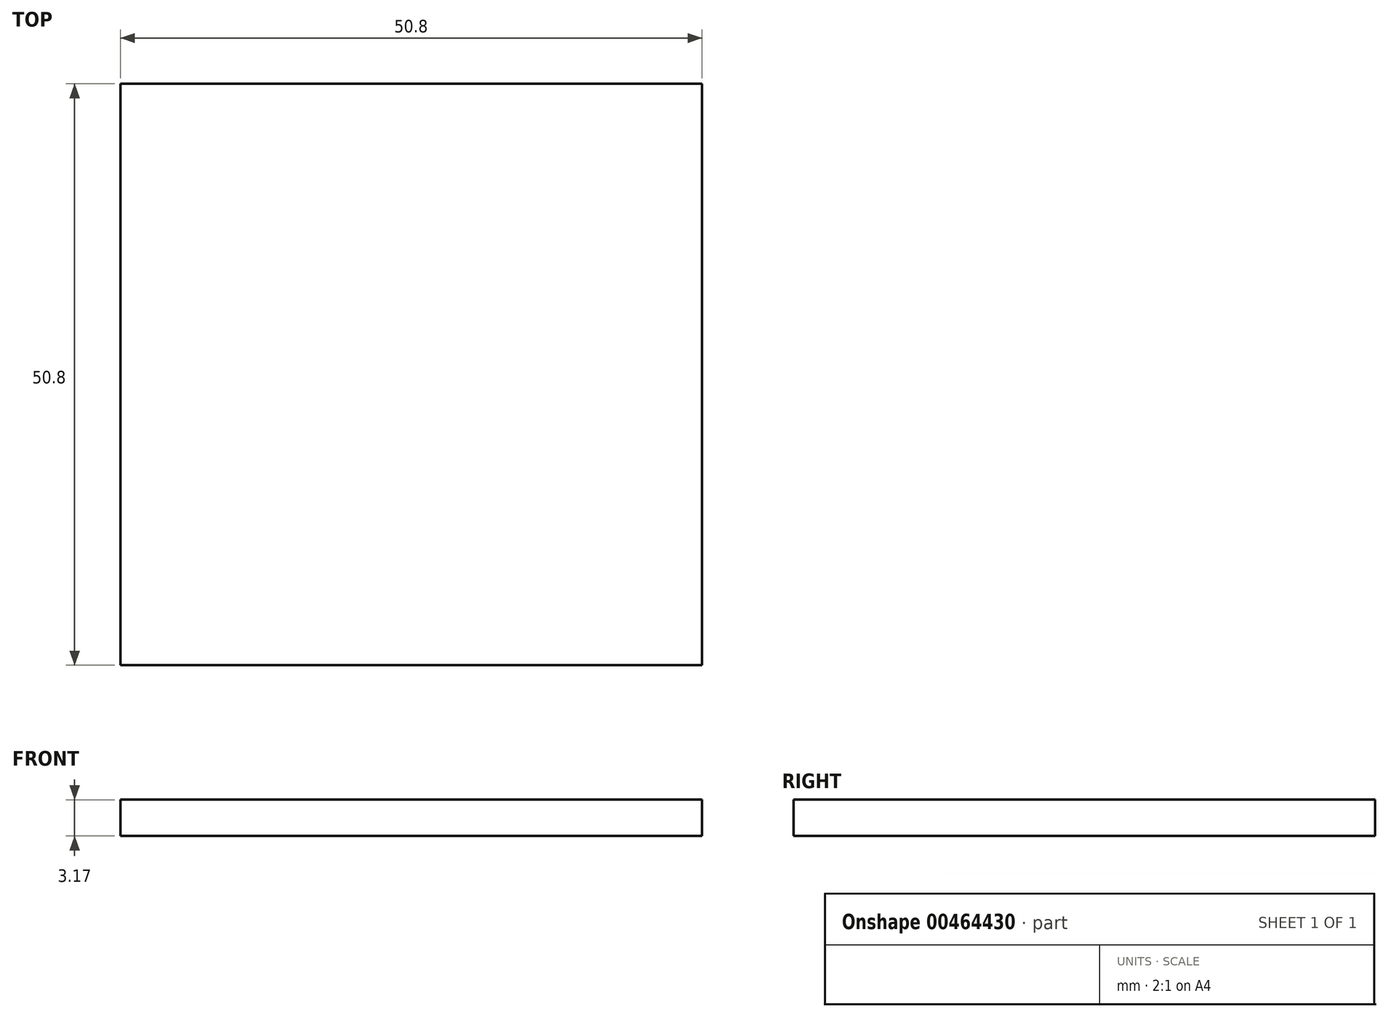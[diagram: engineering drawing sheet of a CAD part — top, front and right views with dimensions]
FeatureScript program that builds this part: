
annotation { "Feature Type Name" : "Feature", "Feature Type Description" : "" }
export const myFeature = defineFeature(function(context is Context, id is Id, definition is map)
    precondition{}
    {
        {
            var Q0;
            Q0=qCreatedBy(makeId("Top.planeOp"),FACE);
            var sketch = newSketch(context, id + "F0", { "sketchPlane" : qUnion([Q0])});
            skLineSegment(sketch, "E0.bottom", {"start": v(25.4, 25.4) * mm, "end": v(-25.4, 25.4) * mm});
            skLineSegment(sketch, "E0.top", {"start": v(25.4, -25.4) * mm, "end": v(-25.4, -25.4) * mm});
            skLineSegment(sketch, "E0.left", {"start": v(25.4, 25.4) * mm, "end": v(25.4, -25.4) * mm});
            skLineSegment(sketch, "E0.right", {"start": v(-25.4, 25.4) * mm, "end": v(-25.4, -25.4) * mm});
            skPoint(sketch, "E0.middle", {"position": v(0, 0) * mm});
            skSolve(sketch);
        }
        {
            var Q0;
            Q0=makeQuery(id+"F0.imprint","IMPRINT",FACE,{"disambiguationData":[TD([[makeQuery(id+"F0.imprint","IMPRINT",EDGE,{"derivedFrom":sQuery(id+"F0.wireOp",EDGE,"E0.bottom")}),1.0]])]});
            extrude(context, id + "F1", {"entities" : qUnion([Q0]), "depth" : 3.17 * mm});
        }
    });
